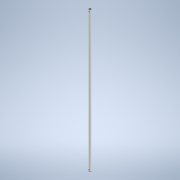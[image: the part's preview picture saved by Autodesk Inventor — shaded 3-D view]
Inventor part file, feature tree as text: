
AUTODESK INVENTOR PART (.ipt)
format: ipt  version: 2022 (Build 260153000, 153)  size: 169,984 bytes
history: native  units: mm
features: extrude x2, sketch x2
ambient origin geometry x8: Origin, YZ Plane, XZ Plane, XY Plane, X Axis, Y Axis, Z Axis, Center Point
bodies: Body1 (feature_tree)
feature tree (4):
  extrude  "Extrusion5"  Depth=7.0mm
  extrude  "Extrusion6"  Depth=10.0mm TaperAngle=0.0deg
  sketch  "Sketch2"  dims[d31=34.456mm d91=7.0mm]
  sketch  "Sketch3"  dims[d92=5.0mm d93=500.0mm d94=0.0mm d95=6.0mm d96=2.0mm d97=6.0mm d98=2.0mm d99=10.0mm d100=10.0mm d101=0.0mm d102=0.0mm]
